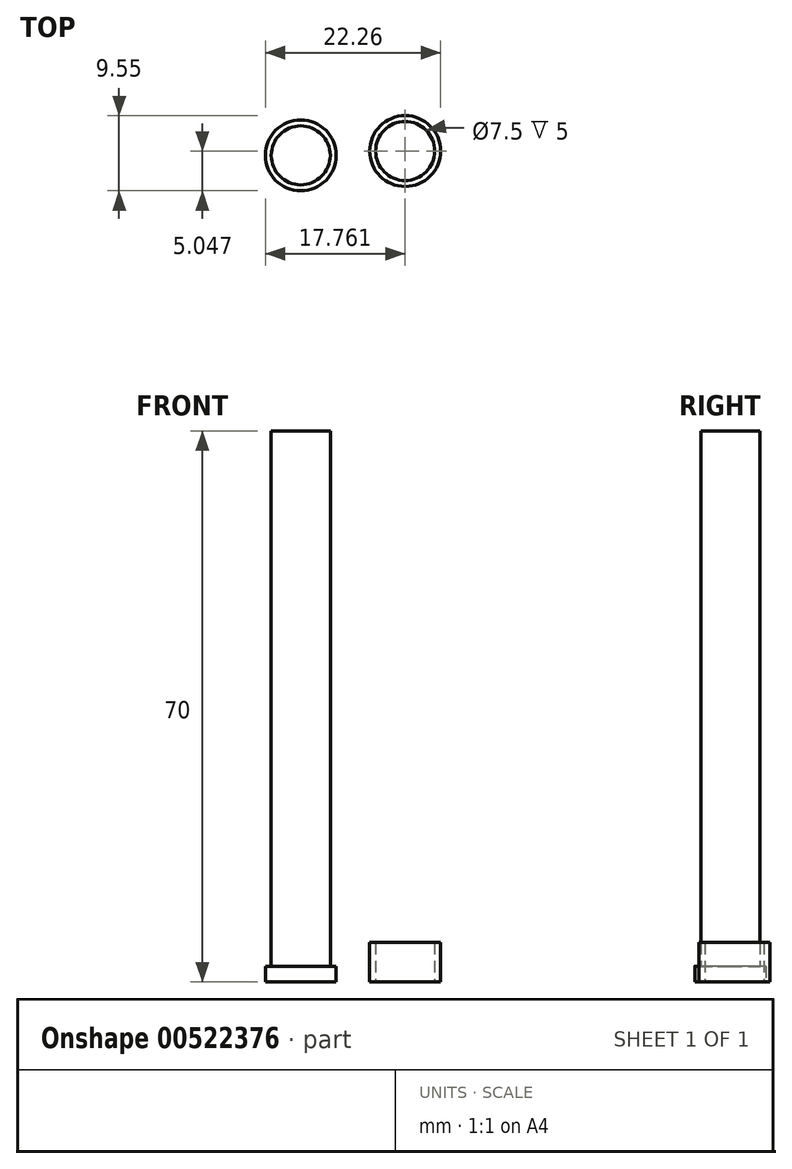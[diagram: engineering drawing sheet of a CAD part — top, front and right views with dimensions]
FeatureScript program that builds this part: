
annotation { "Feature Type Name" : "Feature", "Feature Type Description" : "" }
export const myFeature = defineFeature(function(context is Context, id is Id, definition is map)
    precondition{}
    {
        {
            var Q0;
            Q0=qCreatedBy(makeId("Top.planeOp"),FACE);
            var sketch = newSketch(context, id + "F0", { "sketchPlane" : qUnion([Q0])});
            skCircle(sketch, "E0", {"center": v(0, 0) * mm, "radius": 4.5 * mm});
            skCircle(sketch, "E1", {"center": v(0, 0) * mm, "radius": 3.75 * mm});
            skSolve(sketch);
        }
        {
            var Q0;
            Q0=qCreatedBy(makeId("Top.planeOp"),FACE);
            var sketch = newSketch(context, id + "F1", { "sketchPlane" : qUnion([Q0])});
            skCircle(sketch, "E2", {"center": v(13.26, 0.55) * mm, "radius": 4.5 * mm});
            skCircle(sketch, "E3", {"center": v(13.26, 0.55) * mm, "radius": 3.75 * mm});
            skSolve(sketch);
        }
        {
            var Q0;
            Q0=makeQuery(id+"F0.imprint","IMPRINT",FACE,{"disambiguationData":[TD([[makeQuery(id+"F0.imprint","IMPRINT",EDGE,{"derivedFrom":sQuery(id+"F0.wireOp",EDGE,"E1")}),1.0]])]});
            extrude(context, id + "F2", {"entities" : qUnion([Q0]), "depth" : 70 * mm, "offsetDistance" : 25 * mm});
        }
        {
            var Q0;
            Q0=makeQuery(id+"F0.imprint","IMPRINT",FACE,{"disambiguationData":[TD([[makeQuery(id+"F0.imprint","IMPRINT",EDGE,{"derivedFrom":sQuery(id+"F0.wireOp",EDGE,"E0")}),1.0]])]});
            extrude(context, id + "F3", {"entities" : qUnion([Q0]), "operationType" : NewBodyOperationType.ADD, "depth" : 2 * mm, "offsetDistance" : 25 * mm});
        }
        {
            var Q0;
            Q0=makeQuery(id+"F1.imprint","IMPRINT",FACE,{"disambiguationData":[TD([[makeQuery(id+"F1.imprint","IMPRINT",EDGE,{"derivedFrom":sQuery(id+"F1.wireOp",EDGE,"E2")}),1.0]])]});
            extrude(context, id + "F4", {"entities" : qUnion([Q0]), "depth" : 5 * mm, "offsetDistance" : 25 * mm});
        }
    });
